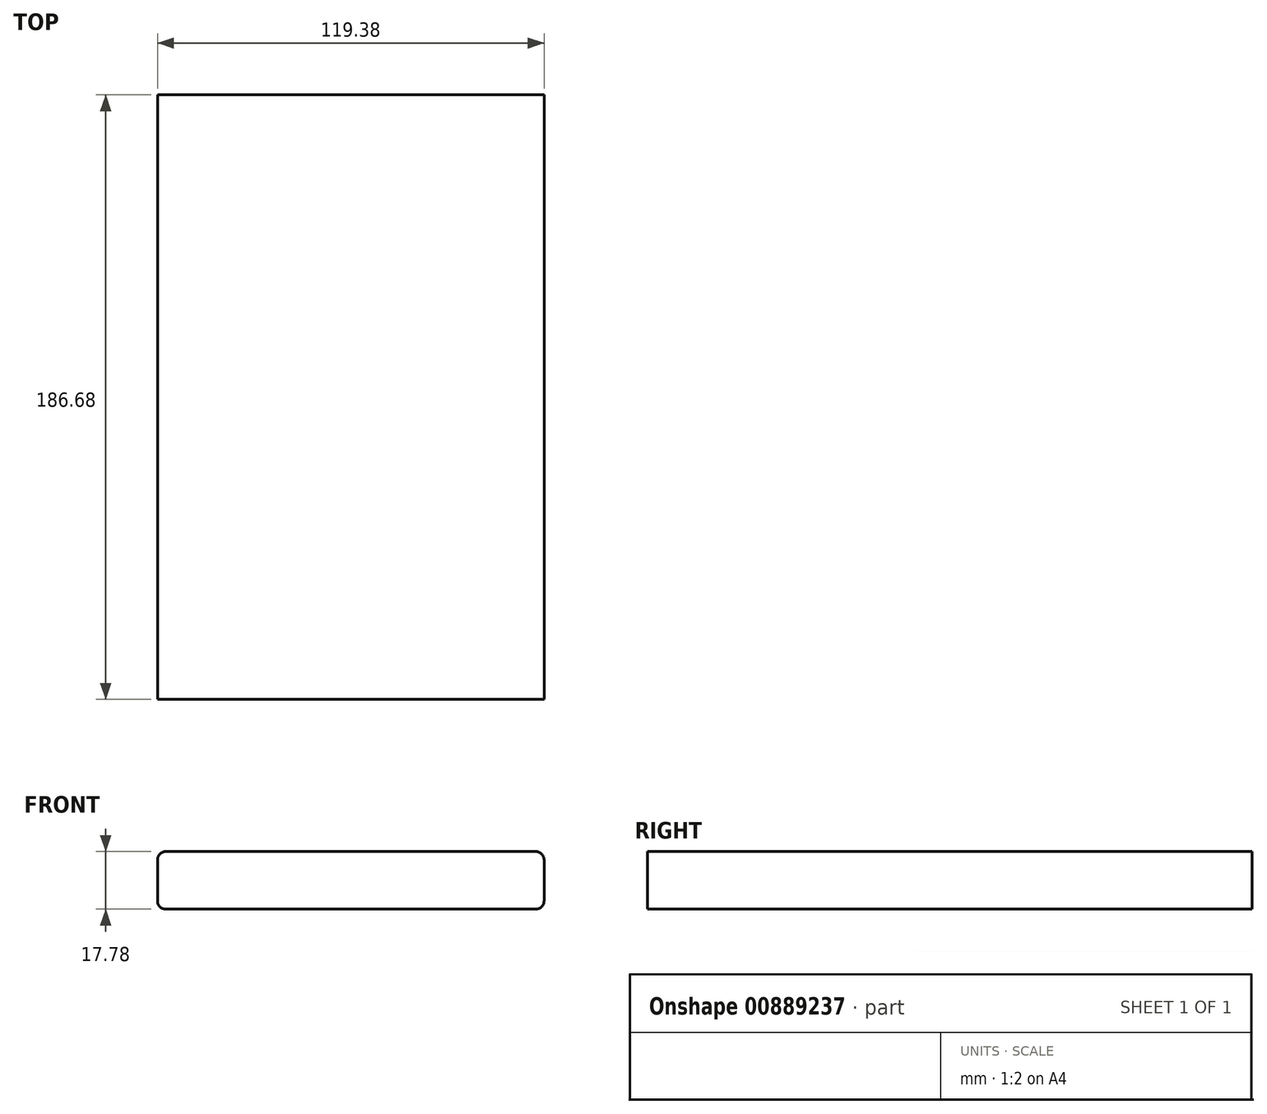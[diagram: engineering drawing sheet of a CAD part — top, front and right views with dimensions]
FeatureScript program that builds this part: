
annotation { "Feature Type Name" : "Feature", "Feature Type Description" : "" }
export const myFeature = defineFeature(function(context is Context, id is Id, definition is map)
    precondition{}
    {
        {
            var Q0;
            Q0=qCreatedBy(makeId("Front.planeOp"),FACE);
            var sketch = newSketch(context, id + "F0", { "sketchPlane" : qUnion([Q0])});
            skLineSegment(sketch, "E0.bottom", {"start": v(59.7, 8.9) * mm, "end": v(-59.7, 8.9) * mm});
            skLineSegment(sketch, "E0.top", {"start": v(59.7, -8.9) * mm, "end": v(-59.7, -8.9) * mm});
            skLineSegment(sketch, "E0.left", {"start": v(59.7, 8.9) * mm, "end": v(59.7, -8.9) * mm});
            skLineSegment(sketch, "E0.right", {"start": v(-59.7, 8.9) * mm, "end": v(-59.7, -8.9) * mm});
            skPoint(sketch, "E0.middle", {"position": v(0, 0) * mm});
            skSolve(sketch);
        }
        {
            var Q0;
            Q0=makeQuery(id+"F0.imprint","IMPRINT",FACE,{"disambiguationData":[TD([[makeQuery(id+"F0.imprint","IMPRINT",EDGE,{"derivedFrom":sQuery(id+"F0.wireOp",EDGE,"E0.bottom")}),1.0]])]});
            extrude(context, id + "F1", {"entities" : qUnion([Q0]), "endBound" : BoundingType.SYMMETRIC, "depth" : 186.7 * mm, "offsetDistance" : 25.4 * mm});
        }
        {
            var Q0;
            Q0=makeQuery(id+"F1.opExtrude","SWEPT_FACE",FACE,{"disambiguationData":[OSD([sQuery(id+"F0.wireOp",EDGE,"E0.bottom")])]});
            var sketch = newSketch(context, id + "F2", { "sketchPlane" : qUnion([Q0])});
            skLineSegment(sketch, "E1.bottom", {"start": v(-53.34, 88.9) * mm, "end": v(53.34, 88.9) * mm});
            skLineSegment(sketch, "E1.top", {"start": v(-53.34, -88.9) * mm, "end": v(53.34, -88.9) * mm});
            skLineSegment(sketch, "E1.left", {"start": v(-53.34, 88.9) * mm, "end": v(-53.34, -88.9) * mm});
            skLineSegment(sketch, "E1.right", {"start": v(53.34, 88.9) * mm, "end": v(53.34, -88.9) * mm});
            skPoint(sketch, "E1.middle", {"position": v(0, 0) * mm});
            skSolve(sketch);
        }
        {
            var Q0;
            Q0=makeQuery(id+"F2.imprint","IMPRINT",FACE,{"disambiguationData":[TD([[makeQuery(id+"F2.imprint","IMPRINT",EDGE,{"derivedFrom":sQuery(id+"F2.wireOp",EDGE,"E1.bottom")}),-1.0]])]});
            extrude(context, id + "F3", {"entities" : qUnion([Q0]), "operationType" : NewBodyOperationType.REMOVE, "oppositeDirection" : true, "depth" : 17.78 * mm, "offsetDistance" : 25.4 * mm});
        }
        {
            var Q0;
            Q0=qCreatedBy(makeId("Top.planeOp"),FACE);
            var sketch = newSketch(context, id + "F4", { "sketchPlane" : qUnion([Q0])});
            skLineSegment(sketch, "E2.bottom", {"start": v(53.34, 88.9) * mm, "end": v(-53.34, 88.9) * mm});
            skLineSegment(sketch, "E2.top", {"start": v(53.34, -88.9) * mm, "end": v(-53.34, -88.9) * mm});
            skLineSegment(sketch, "E2.left", {"start": v(53.34, 88.9) * mm, "end": v(53.34, -88.9) * mm});
            skLineSegment(sketch, "E2.right", {"start": v(-53.34, 88.9) * mm, "end": v(-53.34, -88.9) * mm});
            skPoint(sketch, "E2.middle", {"position": v(0, 0) * mm});
            skSolve(sketch);
        }
        {
            var Q0;
            Q0 = qSketchRegion(id + "F4", true);
            extrude(context, id + "F5", {"entities" : qUnion([Q0]), "operationType" : NewBodyOperationType.ADD, "endBound" : BoundingType.SYMMETRIC, "depth" : 17.78 * mm, "offsetDistance" : 25.4 * mm});
        }
        {
            var Q0;
            Q0=makeQuery(id+"F1.opExtrude","SWEPT_EDGE",EDGE,{"disambiguationData":[OSD([sQuery(id+"F0.wireOp",EDGE,"E0.bottom"),sQuery(id+"F0.wireOp",EDGE,"E0.right")])]});
            var Q1;
            Q1=makeQuery(id+"F1.opExtrude","SWEPT_EDGE",EDGE,{"disambiguationData":[OSD([sQuery(id+"F0.wireOp",EDGE,"E0.top"),sQuery(id+"F0.wireOp",EDGE,"E0.right")])]});
            var Q2;
            Q2=makeQuery(id+"F1.opExtrude","SWEPT_EDGE",EDGE,{"disambiguationData":[OSD([sQuery(id+"F0.wireOp",EDGE,"E0.bottom"),sQuery(id+"F0.wireOp",EDGE,"E0.left")])]});
            var Q3;
            Q3=makeQuery(id+"F1.opExtrude","SWEPT_EDGE",EDGE,{"disambiguationData":[OSD([sQuery(id+"F0.wireOp",EDGE,"E0.top"),sQuery(id+"F0.wireOp",EDGE,"E0.left")])]});
            fillet(context, id + "F6", {"entities" : qUnion([Q0, Q1, Q2, Q3]), "radius" : 2.54 * mm, "tangentPropagation" : true, "allowEdgeOverflow" : false});
        }
    });
